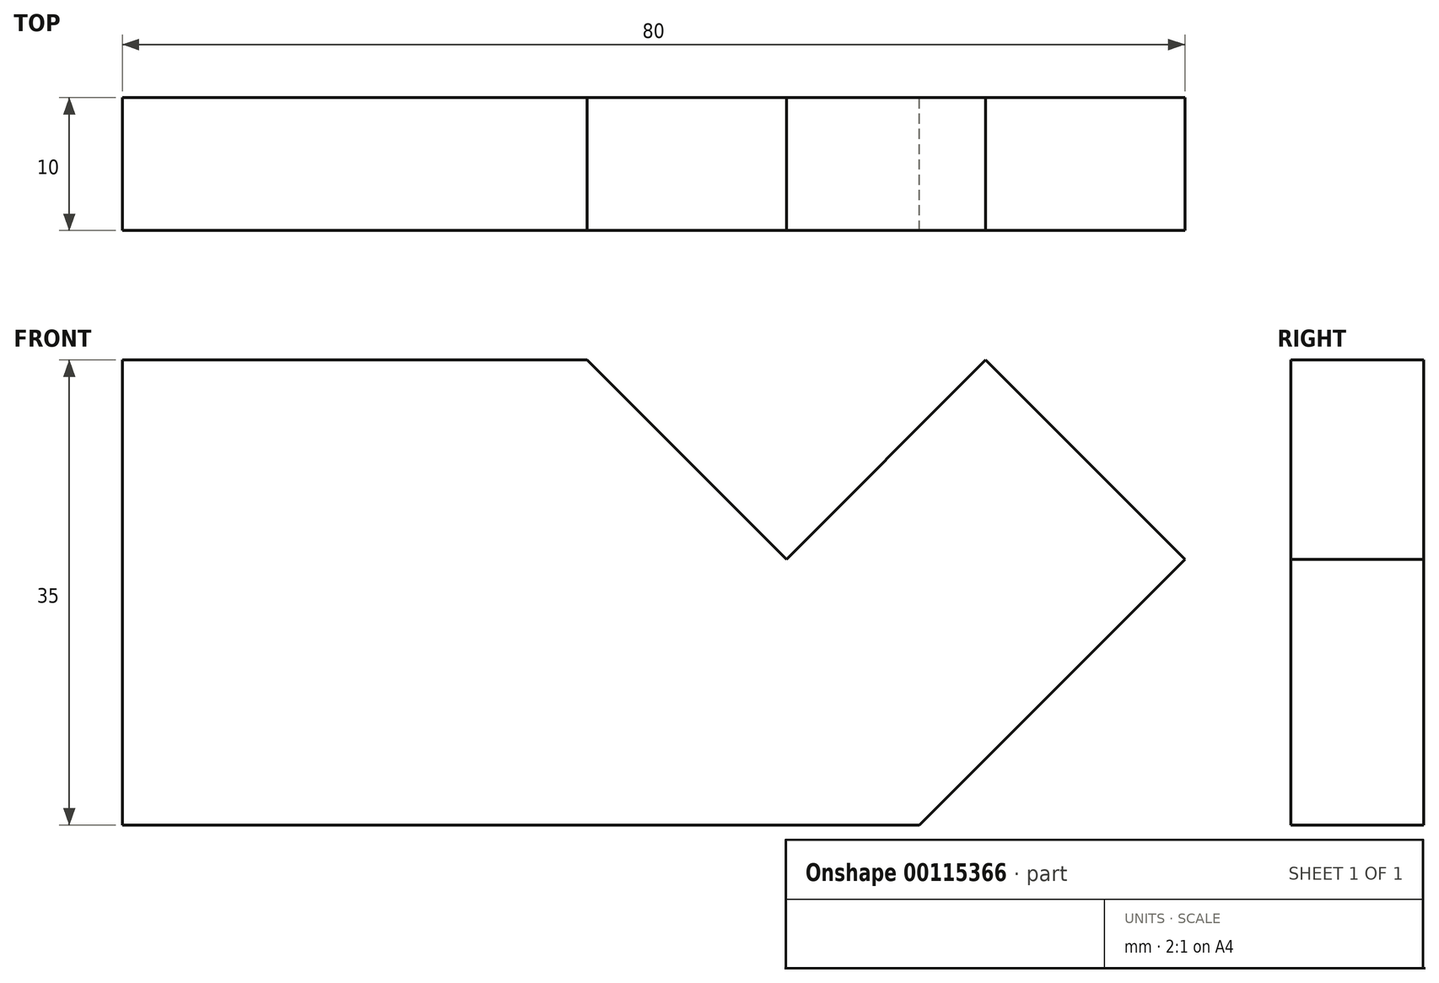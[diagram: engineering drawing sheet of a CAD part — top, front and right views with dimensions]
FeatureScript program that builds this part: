
annotation { "Feature Type Name" : "Feature", "Feature Type Description" : "" }
export const myFeature = defineFeature(function(context is Context, id is Id, definition is map)
    precondition{}
    {
        {
            var Q0;
            Q0=qCreatedBy(makeId("Front.planeOp"),FACE);
            var sketch = newSketch(context, id + "F0", { "sketchPlane" : qUnion([Q0])});
            skLineSegment(sketch, "E0", {"start": v(-55.54, 0) * mm, "end": v(60, 0) * mm, "construction": true});
            skLineSegment(sketch, "E1", {"start": v(0, 65) * mm, "end": v(0, -60.36) * mm, "construction": true});
            skLineSegment(sketch, "E2", {"start": v(0, 35) * mm, "end": v(0, 0) * mm});
            skLineSegment(sketch, "E3", {"start": v(0, 35) * mm, "end": v(70, 35) * mm, "construction": true});
            skLineSegment(sketch, "E4", {"start": v(0, 35) * mm, "end": v(35, 35) * mm});
            skLineSegment(sketch, "E5", {"start": v(35, 35) * mm, "end": v(50, 20) * mm});
            skLineSegment(sketch, "E6", {"start": v(50, 20) * mm, "end": v(65, 35) * mm});
            skLineSegment(sketch, "E7", {"start": v(65, 35) * mm, "end": v(80, 20) * mm});
            skLineSegment(sketch, "E8", {"start": v(80, 20) * mm, "end": v(60, 0) * mm});
            skLineSegment(sketch, "E9", {"start": v(0, 0) * mm, "end": v(60, 0) * mm});
            skSolve(sketch);
        }
        {
            var Q0;
            Q0=makeQuery(id+"F0.imprint","IMPRINT",FACE,{"disambiguationData":[TD([[makeQuery(id+"F0.imprint","IMPRINT",EDGE,{"derivedFrom":sQuery(id+"F0.wireOp",EDGE,"E2")}),1.0]])]});
            extrude(context, id + "F1", {"entities" : qUnion([Q0]), "depth" : 10 * mm});
        }
    });
